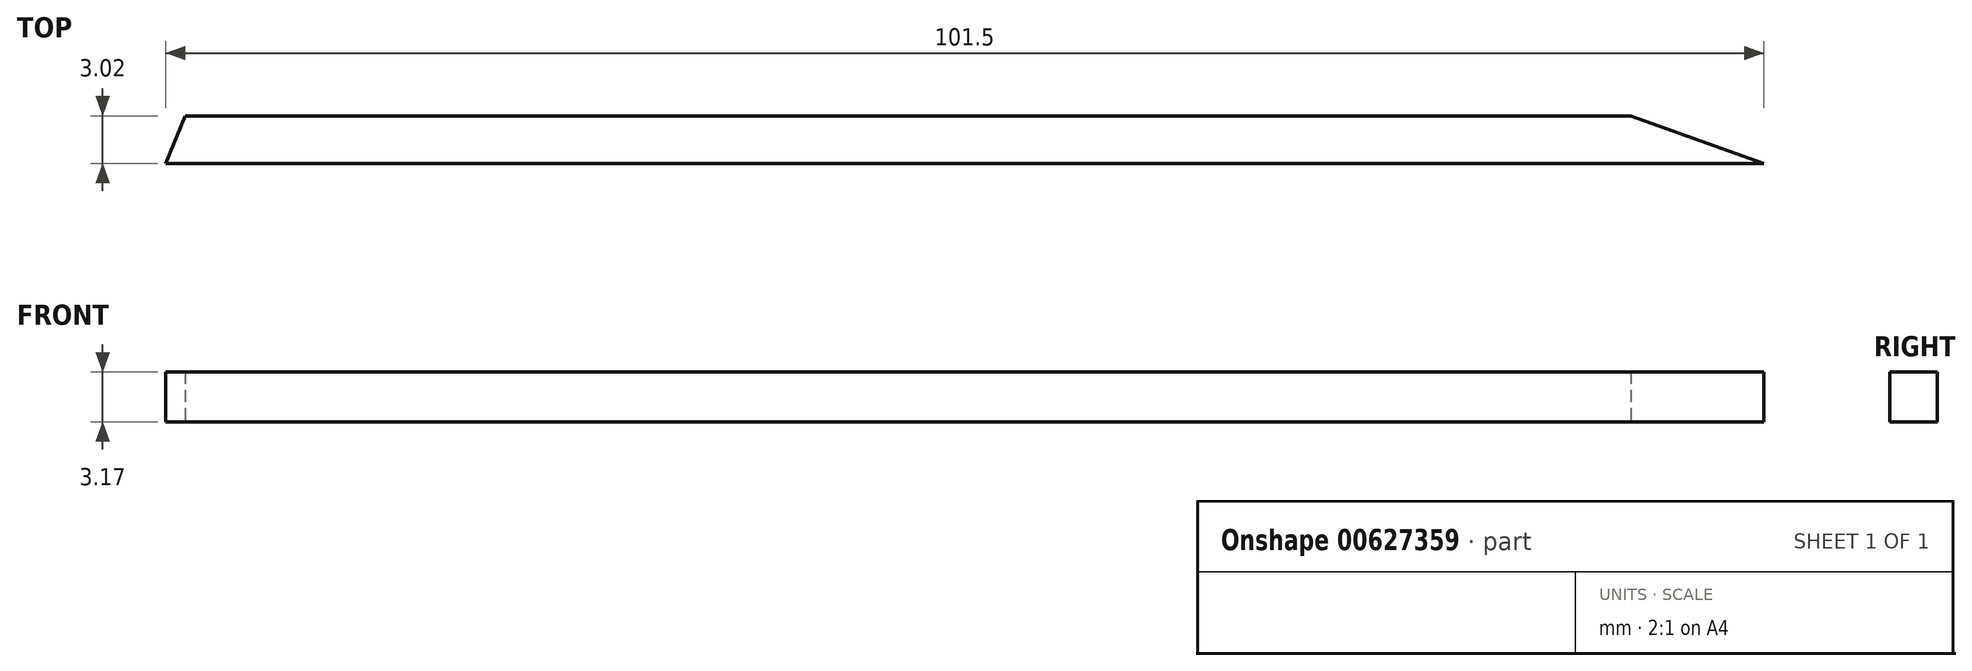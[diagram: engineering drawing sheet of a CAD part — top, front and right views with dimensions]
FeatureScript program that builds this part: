
annotation { "Feature Type Name" : "Feature", "Feature Type Description" : "" }
export const myFeature = defineFeature(function(context is Context, id is Id, definition is map)
    precondition{}
    {
        {
            var Q0;
            Q0=qCreatedBy(makeId("Top.planeOp"),FACE);
            var sketch = newSketch(context, id + "F0", { "sketchPlane" : qUnion([Q0])});
            skLineSegment(sketch, "E0", {"start": v(19.73, 3.02) * mm, "end": v(111.54, 3.02) * mm});
            skLineSegment(sketch, "E1", {"start": v(111.54, 3.02) * mm, "end": v(119.99, 0) * mm});
            skLineSegment(sketch, "E2", {"start": v(119.99, 0) * mm, "end": v(18.49, 0) * mm});
            skLineSegment(sketch, "E3", {"start": v(18.49, 0) * mm, "end": v(19.73, 3.02) * mm});
            skSolve(sketch);
        }
        {
            var Q0;
            Q0=makeQuery(id+"F0.imprint","IMPRINT",FACE,{"disambiguationData":[TD([[makeQuery(id+"F0.imprint","IMPRINT",EDGE,{"derivedFrom":sQuery(id+"F0.wireOp",EDGE,"E0")}),-1.0]])]});
            extrude(context, id + "F1", {"entities" : qUnion([Q0]), "depth" : 3.17 * mm, "offsetDistance" : 25.4 * mm});
        }
    });
